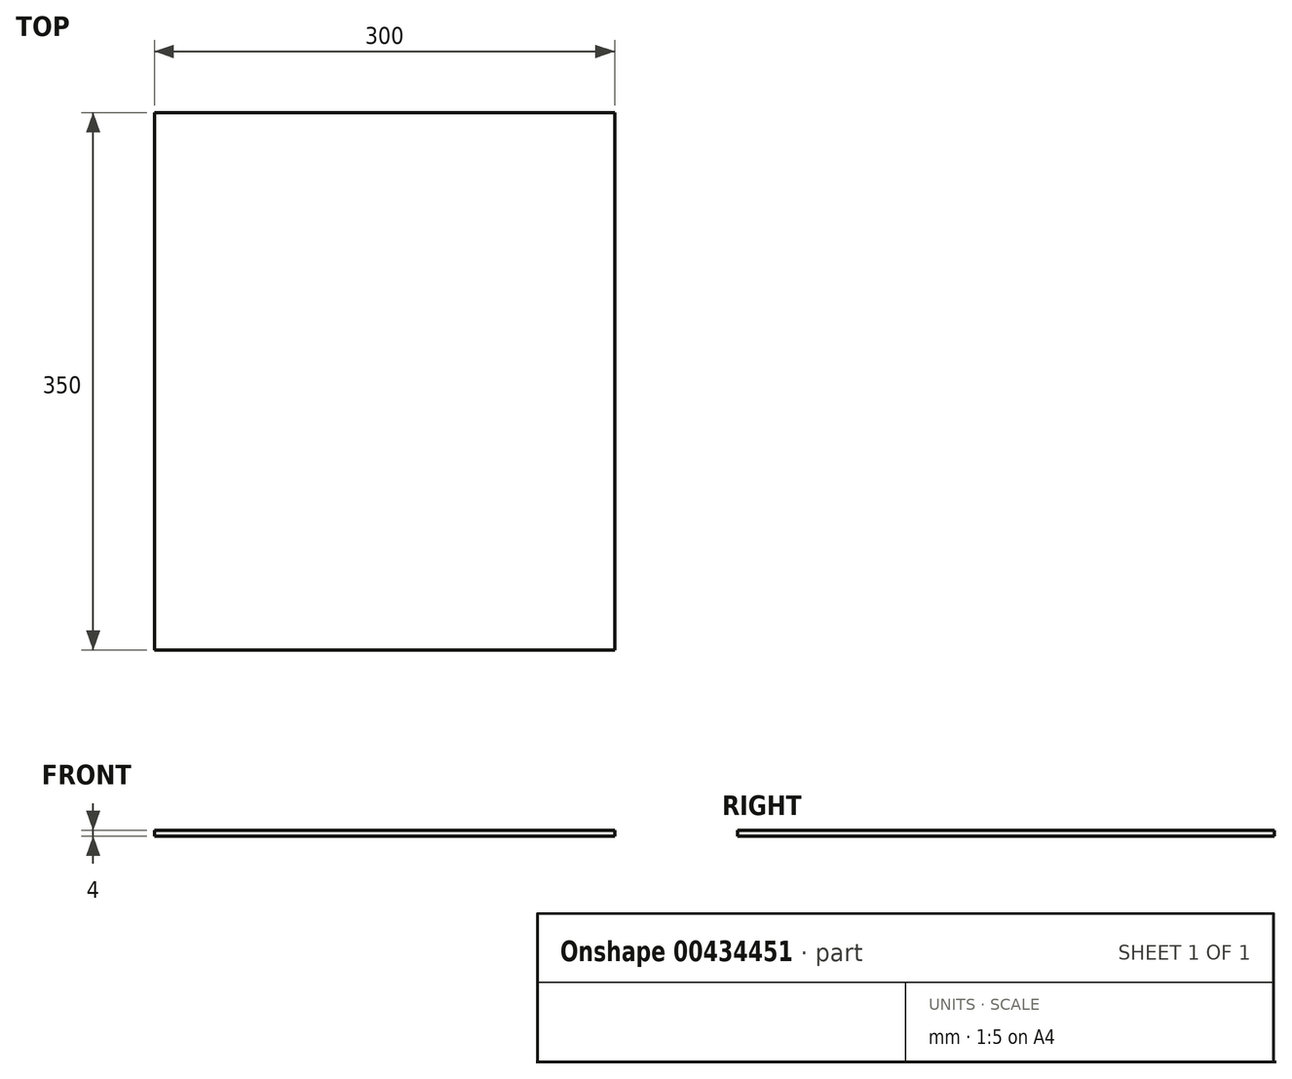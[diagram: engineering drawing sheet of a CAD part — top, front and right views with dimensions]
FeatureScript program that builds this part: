
annotation { "Feature Type Name" : "Feature", "Feature Type Description" : "" }
export const myFeature = defineFeature(function(context is Context, id is Id, definition is map)
    precondition{}
    {
        {
            var Q0;
            Q0=qCreatedBy(makeId("Top.planeOp"),FACE);
            var sketch = newSketch(context, id + "F0", { "sketchPlane" : qUnion([Q0])});
            skLineSegment(sketch, "E0", {"start": v(0, 0) * mm, "end": v(0, 700) * mm});
            skLineSegment(sketch, "E1", {"start": v(0, 700) * mm, "end": v(400, 700) * mm});
            skLineSegment(sketch, "E2", {"start": v(0, 0) * mm, "end": v(0, 0) * mm});
            skLineSegment(sketch, "E3", {"start": v(0, 0) * mm, "end": v(400, 0) * mm});
            skLineSegment(sketch, "E4", {"start": v(400, 0) * mm, "end": v(400, 700) * mm});
            skSolve(sketch);
        }
        {
            var Q0;
            Q0=qSketchRegion(id+"F0",true);
            extrude(context, id + "F1", {"entities" : qUnion([Q0]), "depth" : 4 * mm, "offsetDistance" : 25 * mm});
        }
        {
            var Q0;
            Q0=makeQuery(id+"F1.opExtrude","CAP_FACE",FACE,{"disambiguationData":[OSD([sQuery(id+"F0.wireOp",EDGE,"E0"),sQuery(id+"F0.wireOp",EDGE,"E1"),sQuery(id+"F0.wireOp",EDGE,"sUhJ0AYC-6RA3-jyK1-X7rU-P7NUq0xR7QH3")])],"isStart":false});
            var sketch = newSketch(context, id + "F2", { "sketchPlane" : qUnion([Q0])});
            skLineSegment(sketch, "E5", {"start": v(0, 250) * mm, "end": v(300, 250) * mm});
            skLineSegment(sketch, "E6", {"start": v(300, 250) * mm, "end": v(300, 600) * mm});
            skLineSegment(sketch, "E7", {"start": v(300, 600) * mm, "end": v(0, 600) * mm});
            skLineSegment(sketch, "E8", {"start": v(0, 600) * mm, "end": v(0, 700) * mm});
            skLineSegment(sketch, "E9", {"start": v(0, 700) * mm, "end": v(0, 700) * mm});
            skLineSegment(sketch, "E10", {"start": v(0, 700) * mm, "end": v(0, 600) * mm});
            skLineSegment(sketch, "E11", {"start": v(0, 0) * mm, "end": v(0, 250) * mm});
            skLineSegment(sketch, "E12.trimOffspring", {"start": v(0, 250) * mm, "end": v(0, 0) * mm});
            skLineSegment(sketch, "E13", {"start": v(0, 700) * mm, "end": v(400, 700) * mm});
            skLineSegment(sketch, "E14", {"start": v(400, 700) * mm, "end": v(400, 0) * mm});
            skLineSegment(sketch, "E15", {"start": v(400, 0) * mm, "end": v(0, 0) * mm});
            skSolve(sketch);
        }
        {
            var Q0;
            Q0=qSketchRegion(id+"F2",true);
            extrude(context, id + "F3", {"entities" : qUnion([Q0]), "operationType" : NewBodyOperationType.REMOVE, "endBound" : BoundingType.UP_TO_NEXT, "oppositeDirection" : true, "depth" : 25 * mm, "offsetDistance" : 25 * mm});
        }
    });
